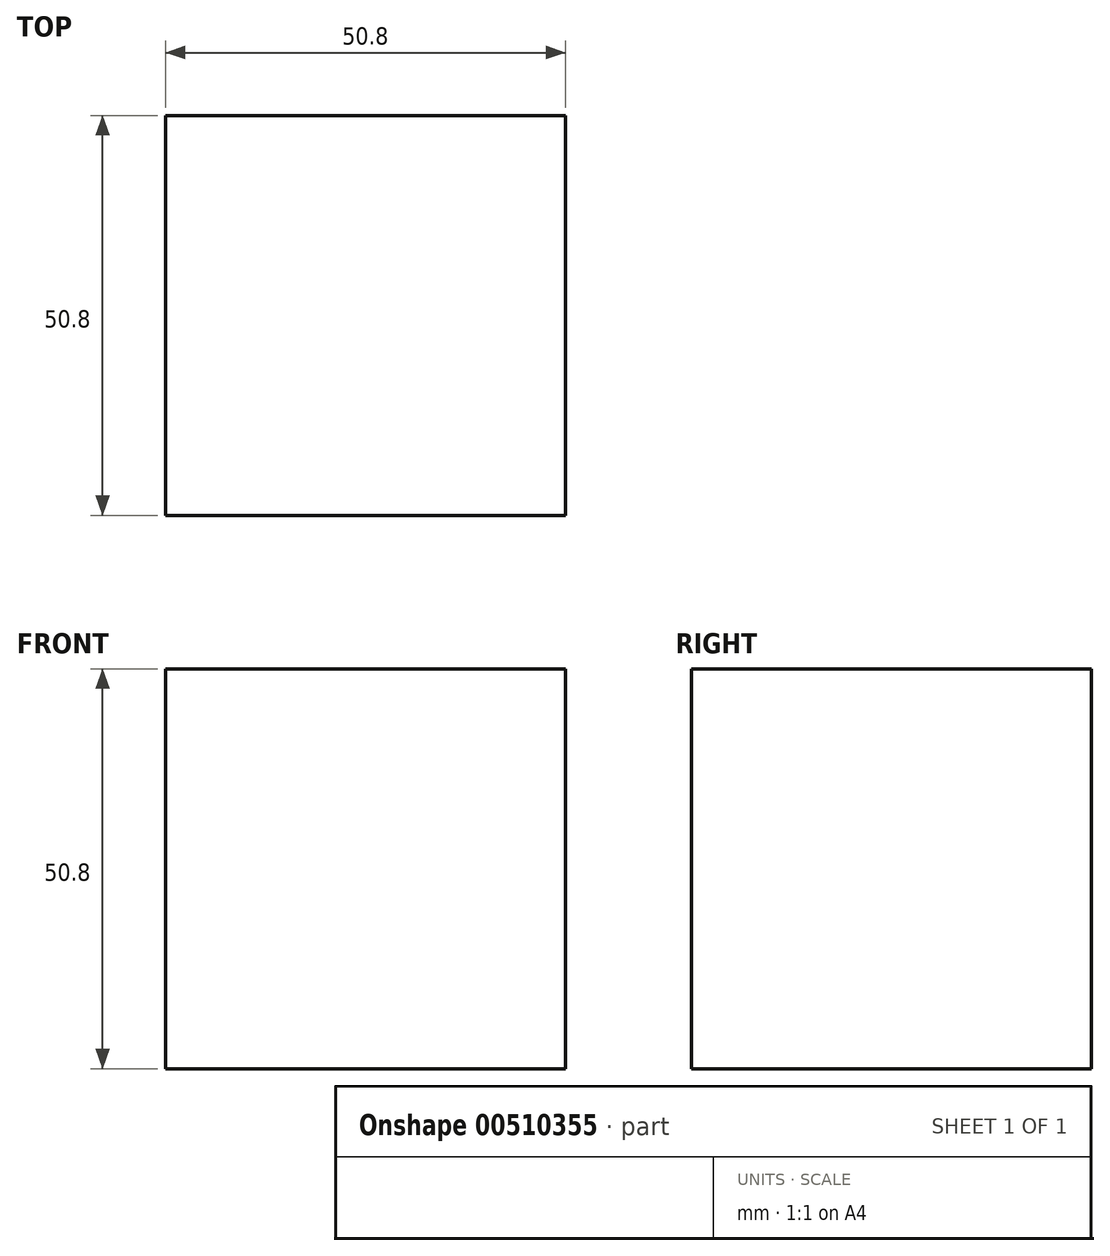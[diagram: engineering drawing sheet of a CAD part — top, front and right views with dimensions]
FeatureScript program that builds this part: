
annotation { "Feature Type Name" : "Feature", "Feature Type Description" : "" }
export const myFeature = defineFeature(function(context is Context, id is Id, definition is map)
    precondition{}
    {
        {
            var Q0;
            Q0=qCreatedBy(makeId("Front.planeOp"),FACE);
            var sketch = newSketch(context, id + "F0", { "sketchPlane" : qUnion([Q0])});
            skLineSegment(sketch, "E0", {"start": v(0, 0) * mm, "end": v(0, 50.8) * mm});
            skLineSegment(sketch, "E1", {"start": v(0, 50.8) * mm, "end": v(50.8, 50.8) * mm});
            skLineSegment(sketch, "E2", {"start": v(50.8, 50.8) * mm, "end": v(50.8, 0) * mm});
            skLineSegment(sketch, "E3", {"start": v(50.8, 0) * mm, "end": v(0, 0) * mm});
            skSolve(sketch);
        }
        {
            var Q0;
            Q0=makeQuery(id+"F0.imprint","IMPRINT",FACE,{"disambiguationData":[TD([[makeQuery(id+"F0.imprint","IMPRINT",EDGE,{"derivedFrom":sQuery(id+"F0.wireOp",EDGE,"E0")}),-1.0]])]});
            extrude(context, id + "F1", {"entities" : qUnion([Q0]), "depth" : 50.8 * mm});
        }
    });
